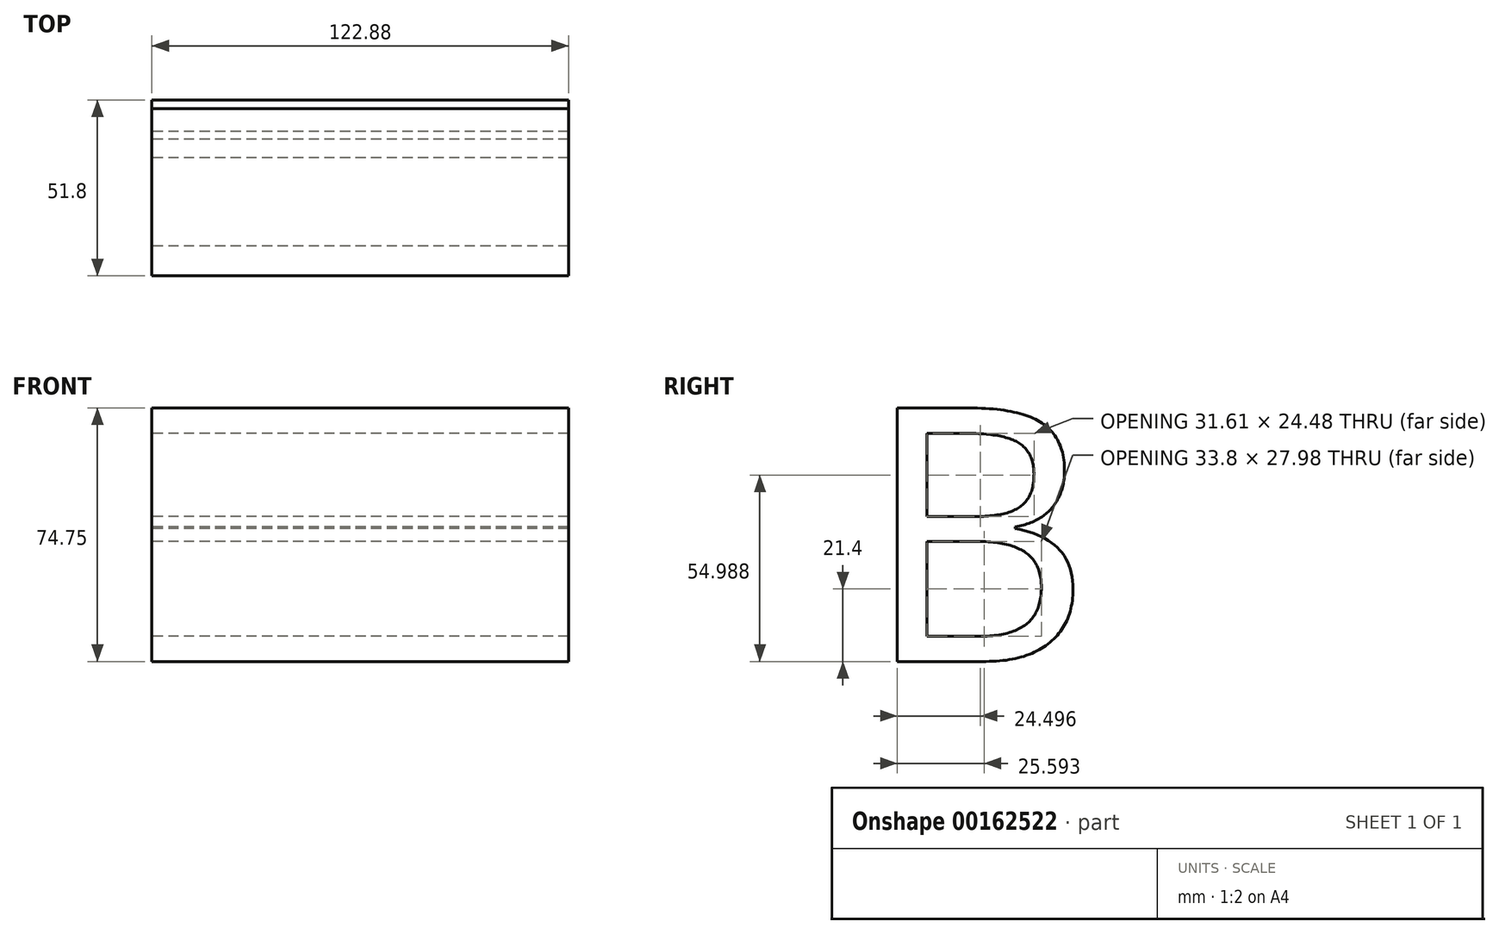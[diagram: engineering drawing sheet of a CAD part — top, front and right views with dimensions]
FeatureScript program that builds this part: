
annotation { "Feature Type Name" : "Feature", "Feature Type Description" : "" }
export const myFeature = defineFeature(function(context is Context, id is Id, definition is map)
    precondition{}
    {
        {
            var Q0;
            Q0=qCreatedBy(makeId("Front.planeOp"),FACE);
            var sketch = newSketch(context, id + "F0", { "sketchPlane" : qUnion([Q0])});
            skText(sketch, "E0", { "text": "D", "fontName": "OpenSans-Regular.ttf"});
            const initialGuessF0  = {"E0": [0, 0, 1, 0, 0.07539]};
            skSetInitialGuess(sketch, initialGuessF0);
            skSolve(sketch);
        }
        {
            var Q0;
            Q0=qCreatedBy(makeId("Right.planeOp"),FACE);
            var sketch = newSketch(context, id + "F1", { "sketchPlane" : qUnion([Q0])});
            skText(sketch, "E1", { "text": "B", "fontName": "OpenSans-Regular.ttf"});
            const initialGuessF1  = {"E1": [0, 0, 1, 0, 0.07539]};
            skSetInitialGuess(sketch, initialGuessF1);
            skSolve(sketch);
        }
        {
            var Q0;
            Q0=makeQuery(id+"F1.imprint","IMPRINT",FACE,{"disambiguationData":[TD([[makeQuery(id+"F1.imprint","IMPRINT",EDGE,{"derivedFrom":sQuery(id+"F1.wireOp",EDGE,"E1.sketch_text.stroke-0")}),-1.0]])]});
            extrude(context, id + "F2", {"entities" : qUnion([Q0]), "depth" : 79.04 * mm});
        }
        {
            var Q0;
            Q0=makeQuery(id+"F1.imprint","IMPRINT",FACE,{"disambiguationData":[TD([[makeQuery(id+"F1.imprint","IMPRINT",EDGE,{"derivedFrom":sQuery(id+"F1.wireOp",EDGE,"E1.sketch_text.stroke-0")}),-1.0]])]});
            extrude(context, id + "F3", {"entities" : qUnion([Q0]), "operationType" : NewBodyOperationType.ADD, "depth" : 122.88 * mm});
        }
    });
